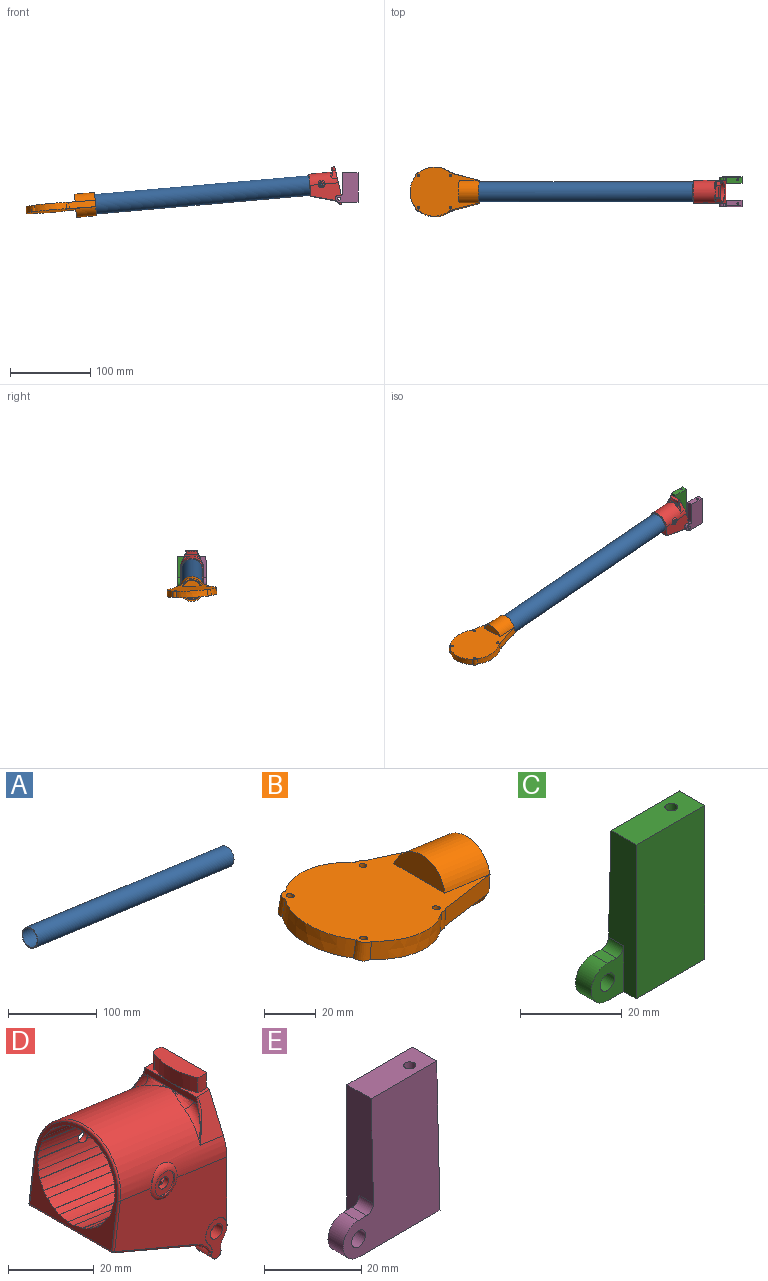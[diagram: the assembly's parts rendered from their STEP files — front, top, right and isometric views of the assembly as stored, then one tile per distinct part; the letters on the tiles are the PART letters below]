
ASSEMBLY  parts=5 mates=2
PART A: 4 faces, bbox 316.9x25x68.8 mm
  f0: cylinder r=12.5mm len=316.9mm, axis (0.99,0,-0.14), area 24857.9mm2, adj f1,f3
  f1: plane 25x24.76mm, normal (0.99,0,-0.14), area 75.4mm2, adj f0,f2
  f2: cylinder r=11.5mm len=316.62mm, axis (0.99,0,-0.14), area 22869.2mm2, adj f1,f3
  f3: plane 25x24.76mm, normal (-0.99,0,0.14), area 75.4mm2, adj f0,f2
PART B: 22 faces, bbox 88.7x62x32.2 mm
  f0: plane 85.74x61.16mm, normal (0.14,0,0.99), area 3234.5mm2, adj f2,f3,f4,f5,f6,f7,f8,f9
  f1: plane 86.15x62mm, normal (-0.14,0,-0.99), area 3325.5mm2, adj f2,f3,f4,f5,f6,f7,f8,f9
  f2: cone r=4mm half-angle=3deg, axis (-0.14,0,-0.99), area 59.2mm2, adj f0,f1,f3,f14
  f3: cone r=31mm half-angle=3deg, axis (-0.14,0,-0.99), area 337.2mm2, adj f0,f1,f2,f4
  f4: cone r=4mm half-angle=3deg, axis (-0.14,0,-0.99), area 59.2mm2, adj f0,f1,f3,f5
  f5: cone r=31mm half-angle=3deg, axis (-0.14,0,-0.99), area 337.2mm2, adj f0,f1,f4,f6
  f6: cone r=4mm half-angle=3deg, axis (-0.14,0,-0.99), area 30.1mm2, adj f0,f1,f5,f7
  f7: plane 33.82x12.55mm, normal (0.25,-0.97,0.02), area 274mm2, adj f0,f1,f6,f8
  f8: plane 29x28.72mm, normal (0.99,0,-0.14), area 169.2mm2, adj f0,f1,f7,f9,f16,f19,f21
  f9: plane 33.82x12.55mm, normal (0.25,0.97,0.02), area 274mm2, adj f0,f1,f8,f10
  f10: cone r=4mm half-angle=3deg, axis (-0.14,0,-0.99), area 30.1mm2, adj f0,f1,f9,f14
  f11: cylinder r=1.5mm len=8.34mm, axis (-0.14,0,-0.99), area 75.4mm2, adj f0,f1
  f12: cylinder r=1.5mm len=8.34mm, axis (-0.14,0,-0.99), area 75.4mm2, adj f0,f1
  f13: cylinder r=1.5mm len=8.34mm, axis (-0.14,0,-0.99), area 75.4mm2, adj f0,f1
  f14: cone r=31mm half-angle=3deg, axis (-0.14,0,-0.99), area 337.2mm2, adj f0,f1,f2,f10
  f15: cylinder r=1.5mm len=8.34mm, axis (-0.14,0,-0.99), area 75.4mm2, adj f0,f1
  f16: cylinder r=14.5mm len=27.87mm, axis (-0.99,0,0.14), area 936.2mm2, adj f1,f8,f17
  f17: plane 27.87x10.4mm, normal (-0.99,0,0.14), area 215.7mm2, adj f1,f16
  f18: plane 27.87x10.4mm, normal (-0.99,0,0.14), area 215.7mm2, adj f0,f19
  f19: cylinder r=14.5mm len=27.87mm, axis (-0.99,0,0.14), area 936.2mm2, adj f0,f8,f18
  f20: plane 25x24.76mm, normal (0.99,0,-0.14), area 490.9mm2, adj f21
  f21: cylinder r=12.5mm len=28.03mm, axis (0.99,0,-0.14), area 1845.7mm2, adj f8,f20
PART C: 15 faces, bbox 28x8x37 mm
  f0: cylinder r=2mm len=4.43mm, axis (0,-1,0), area 55mm2, adj f3,f9
  f1: plane 37x19mm, normal (0,-1,0), area 703mm2, adj f4,f5,f6,f8
  f2: cylinder r=4.5mm len=9mm, axis (0,-1,0), area 61.9mm2, adj f3,f7,f8,f9
  f3: plane 37x28mm, normal (0,1,0.03), area 763.9mm2, adj f0,f2,f4,f5,f6,f7,f8,f10
  f4: plane 37x8mm, normal (1,0,0), area 277.5mm2, adj f1,f3,f5,f8
  f5: plane 19x7mm, normal (0,0,1), area 128.1mm2, adj f1,f3,f4,f6,f14
  f6: plane 37x7.7mm, normal (-1,0,0), area 229.6mm2, adj f1,f3,f5,f8,f9,f10
  f7: plane 4.26x2.5mm, normal (0,0,1), area 10.6mm2, adj f2,f3,f9,f10
  f8: plane 23.5x8mm, normal (0,0,-1), area 167.3mm2, adj f1,f2,f3,f4,f6,f9,f12
  f9: plane 11x9mm, normal (0,-1,0), area 60.6mm2, adj f0,f2,f6,f7,f8,f10
  f10: cylinder r=2mm len=4.26mm, axis (0,1,0), area 13.3mm2, adj f3,f6,f7,f9
  f11: cone r=0mm half-angle=59deg, axis (0,0,-1), area 5.7mm2, adj f12
  f12: cylinder r=1.25mm len=13.5mm, axis (0,0,-1), area 106mm2, adj f8,f11
  f13: cone r=0mm half-angle=59deg, axis (0,0,1), area 5.7mm2, adj f14
  f14: cylinder r=1.25mm len=13.5mm, axis (0,0,1), area 106mm2, adj f5,f13
PART D: 138 faces, bbox 40.7x34.8x48 mm
  f0: cylinder r=10mm len=5.84mm, axis (0,1,0), area 37.2mm2, adj f1,f36,f119,f130
  f1: cylinder r=1.5mm len=5.1mm, axis (0,1,0), area 23.1mm2, adj f0,f2,f40,f41,f119,f130
  f2: cylinder r=4mm len=5.1mm, axis (0,1,0), area 19.4mm2, adj f1,f35,f41,f119
  f3: plane 13.62x1.92mm, normal (0.14,-0.08,0.99), area 1.4mm2, adj f21,f54,f68,f116
  f4: cylinder r=12.6mm len=13.9mm, axis (-0.99,0,0.14), area 27.5mm2, adj f27,f67,f69,f116
  f5: plane 13.62x1.92mm, normal (-0.14,-0.08,-0.99), area 1.4mm2, adj f22,f54,f68,f116
  f6: plane 13.62x1.92mm, normal (-0.14,0.08,-0.99), area 1.4mm2, adj f7,f13,f27,f117
  f7: cylinder r=12.6mm len=13.9mm, axis (-0.99,0,0.14), area 27.5mm2, adj f6,f8,f27,f117
  f8: plane 13.62x1.92mm, normal (0.14,0.08,0.99), area 1.4mm2, adj f7,f14,f27,f117
  f9: cylinder r=14mm len=37.01mm, axis (-0.99,0,0.14), area 1218.4mm2, adj f28,f29,f30,f52,f53,f109,f110,f114
  f10: cylinder r=12.5mm len=29.79mm, axis (-0.99,0,0.14), area 87.7mm2, adj f27,f54,f57,f100
  f11: cylinder r=12.5mm len=29.93mm, axis (-0.99,0,0.14), area 87.7mm2, adj f27,f54,f97,f102
  f12: cylinder r=12.5mm len=30.05mm, axis (-0.99,0,0.14), area 87.7mm2, adj f27,f54,f94,f99
  f13: cylinder r=12.5mm len=30.11mm, axis (-0.99,0,0.14), area 86.7mm2, adj f6,f27,f54,f91,f96,f117
  f14: cylinder r=12.5mm len=30.11mm, axis (-0.99,0,0.14), area 86.6mm2, adj f8,f27,f54,f88,f93,f117
  f15: cylinder r=12.5mm len=30.05mm, axis (-0.99,0,0.14), area 87.7mm2, adj f27,f54,f85,f90
  f16: cylinder r=12.5mm len=29.93mm, axis (-0.99,0,0.14), area 87.7mm2, adj f27,f54,f82,f87
  f17: cylinder r=12.5mm len=29.79mm, axis (-0.99,0,0.14), area 87.7mm2, adj f27,f54,f79,f84
  f18: cylinder r=12.5mm len=29.79mm, axis (-0.99,0,0.14), area 87.7mm2, adj f27,f54,f76,f81
  f19: cylinder r=12.5mm len=29.93mm, axis (-0.99,0,0.14), area 87.7mm2, adj f27,f54,f73,f78
  f20: cylinder r=12.5mm len=30.05mm, axis (-0.99,0,0.14), area 87.7mm2, adj f27,f54,f70,f75
  f21: cylinder r=12.5mm len=30.11mm, axis (-0.99,0,0.14), area 86.6mm2, adj f3,f27,f54,f67,f72,f116
  f22: cylinder r=12.5mm len=30.11mm, axis (-0.99,0,0.14), area 86.7mm2, adj f5,f27,f54,f64,f69,f116
  f23: cylinder r=12.5mm len=30.05mm, axis (-0.99,0,0.14), area 87.7mm2, adj f27,f54,f61,f66
  f24: cylinder r=12.5mm len=29.93mm, axis (-0.99,0,0.14), area 87.7mm2, adj f27,f54,f58,f63
  f25: cylinder r=12.5mm len=29.79mm, axis (-0.99,0,0.14), area 87.7mm2, adj f27,f54,f55,f60
  f26: cylinder r=12.5mm len=25.51mm, axis (-0.99,0,0.14), area 279mm2, adj f106,f137
  f27: plane 27x26.85mm, normal (-0.99,0,0.14), area 159.8mm2, adj f4,f6,f7,f8,f10,f11,f12,f13
  f28: plane 36.95x29.79mm, normal (0,1,0), area 620.1mm2, adj f9,f30,f35,f40,f109,f130,f133,f136
  f29: plane 36.95x29.79mm, normal (0,-1,0), area 620.1mm2, adj f9,f30,f35,f43,f115,f127,f128,f131
  f30: plane 40.17x28.02mm, normal (1,0,0), area 451.6mm2, adj f9,f28,f29,f31,f34,f35,f45,f49
  f31: plane 8.53x4.52mm, normal (0,0,1), area 7.9mm2, adj f30,f32,f48,f49,f53,f125
  f32: plane 17.95x1.83mm, normal (-1,0,0), area 29.3mm2, adj f31,f33,f34,f51,f122,f123,f125,f126
  f33: plane 1.3x0.8mm, normal (-0.99,0,0.14), area 0.4mm2, adj f32,f124,f125
  f34: plane 8.53x4.52mm, normal (0,0,1), area 7.8mm2, adj f30,f32,f45,f46,f47,f48,f52,f126
  f35: cylinder r=3.5mm len=28.2mm, axis (0,1,0), area 179.8mm2, adj f2,f28,f29,f30,f39,f40,f41,f43
  f36: plane 31.51x27mm, normal (-0.39,0,-0.92), area 876.8mm2, adj f0,f37,f118,f119,f120,f128,f132,f133
  f37: cylinder r=10mm len=5.84mm, axis (0,1,0), area 37.2mm2, adj f36,f38,f120,f127
  f38: cylinder r=1.5mm len=5.1mm, axis (0,1,0), area 23.1mm2, adj f37,f39,f43,f44,f120,f127
  f39: cylinder r=4mm len=5.1mm, axis (0,1,0), area 19.4mm2, adj f35,f38,f44,f120
  f40: cylinder r=4mm len=3.5mm, axis (0,1,0), area 0.4mm2, adj f1,f28,f35,f41,f130
  f41: plane 11.2x7mm, normal (0,1,0), area 38.3mm2, adj f1,f2,f35,f40,f42
  f42: cylinder r=2mm len=28.2mm, axis (0,1,0), area 354.4mm2, adj f41,f44
  f43: cylinder r=4mm len=3.5mm, axis (0,1,0), area 0.4mm2, adj f29,f35,f38,f44,f127
  f44: plane 11.2x7mm, normal (0,-1,0), area 38.3mm2, adj f35,f38,f39,f42,f43
  f45: cylinder r=3.19mm len=4.25mm, axis (0,0,-1), area 13.3mm2, adj f30,f34,f46,f50
  f46: cylinder r=18.27mm len=4.25mm, axis (0,0,-1), area 1mm2, adj f34,f45,f47,f50
  f47: cylinder r=0.45mm len=4.25mm, axis (0,0,-1), area 4.2mm2, adj f34,f46,f48,f50
  f48: cylinder r=18.27mm len=13.53mm, axis (0,0,-1), area 58.9mm2, adj f31,f34,f47,f49,f50
  f49: cylinder r=3.19mm len=4.25mm, axis (0,0,-1), area 13.3mm2, adj f30,f31,f48,f50
  f50: plane 15.25x4.5mm, normal (0,0,1), area 59.8mm2, adj f30,f45,f46,f47,f48,f49
  f51: plane 1.3x0.8mm, normal (-0.99,0,0.14), area 0.4mm2, adj f32,f121,f126
  f52: plane 10.9x7.66mm, normal (0.05,0.92,0.39), area 60.1mm2, adj f9,f30,f34,f126
  f53: plane 10.9x7.66mm, normal (0.05,-0.92,0.39), area 60.1mm2, adj f9,f30,f31,f125
  f54: plane 25.2x24.95mm, normal (-0.99,0,0.14), area 78.6mm2, adj f3,f5,f10,f11,f12,f13,f14,f15
  f55: plane 29.72x4.27mm, normal (0.01,1,0.08), area 3mm2, adj f25,f27,f54,f56
  f56: cylinder r=12.6mm len=29.71mm, axis (-0.99,0,0.14), area 60.1mm2, adj f27,f54,f55,f57
  f57: plane 29.72x4.27mm, normal (0.01,-1,0.08), area 3mm2, adj f10,f27,f54,f56
  f58: plane 29.72x4.26mm, normal (0.06,0.89,0.45), area 3mm2, adj f24,f27,f54,f59
  f59: cylinder r=12.6mm len=29.81mm, axis (-0.99,0,0.14), area 60.1mm2, adj f27,f54,f58,f60
  f60: plane 29.72x4.27mm, normal (-0.04,-0.95,-0.31), area 3mm2, adj f25,f27,f54,f59
  f61: plane 29.72x4.24mm, normal (0.11,0.65,0.75), area 3mm2, adj f23,f27,f54,f62
  f62: cylinder r=12.6mm len=29.91mm, axis (-0.99,0,0.14), area 60.1mm2, adj f27,f54,f61,f63
  f63: plane 29.72x4.25mm, normal (-0.09,-0.76,-0.64), area 3mm2, adj f24,f27,f54,f62
  f64: plane 29.71x4.21mm, normal (0.13,0.31,0.94), area 3mm2, adj f22,f27,f54,f65
  f65: cylinder r=12.6mm len=29.97mm, axis (-0.99,0,0.14), area 60.1mm2, adj f27,f54,f64,f66
  f66: plane 29.71x4.22mm, normal (-0.12,-0.45,-0.88), area 3mm2, adj f23,f27,f54,f65
  f67: plane 13.62x1.92mm, normal (0.14,-0.08,0.99), area 1.4mm2, adj f4,f21,f27,f116
  f68: cylinder r=12.6mm len=13.9mm, axis (-0.99,0,0.14), area 27.5mm2, adj f3,f5,f54,f116
  f69: plane 13.62x1.92mm, normal (-0.14,-0.08,-0.99), area 1.4mm2, adj f4,f22,f27,f116
  f70: plane 29.71x4.22mm, normal (0.12,-0.45,0.88), area 3mm2, adj f20,f27,f54,f71
  f71: cylinder r=12.6mm len=29.97mm, axis (-0.99,0,0.14), area 60.1mm2, adj f27,f54,f70,f72
  f72: plane 29.71x4.21mm, normal (-0.13,0.31,-0.94), area 3mm2, adj f21,f27,f54,f71
  f73: plane 29.72x4.25mm, normal (0.09,-0.76,0.64), area 3mm2, adj f19,f27,f54,f74
  f74: cylinder r=12.6mm len=29.91mm, axis (-0.99,0,0.14), area 60.1mm2, adj f27,f54,f73,f75
  f75: plane 29.72x4.24mm, normal (-0.11,0.65,-0.75), area 3mm2, adj f20,f27,f54,f74
  f76: plane 29.72x4.27mm, normal (0.04,-0.95,0.31), area 3mm2, adj f18,f27,f54,f77
  f77: cylinder r=12.6mm len=29.81mm, axis (-0.99,0,0.14), area 60.1mm2, adj f27,f54,f76,f78
  f78: plane 29.72x4.26mm, normal (-0.06,0.89,-0.45), area 3mm2, adj f19,f27,f54,f77
  f79: plane 29.72x4.27mm, normal (-0.01,-1,-0.08), area 3mm2, adj f17,f27,f54,f80
  f80: cylinder r=12.6mm len=29.71mm, axis (-0.99,0,0.14), area 60.1mm2, adj f27,f54,f79,f81
  f81: plane 29.72x4.27mm, normal (-0.01,1,-0.08), area 3mm2, adj f18,f27,f54,f80
  f82: plane 29.72x4.26mm, normal (-0.06,-0.89,-0.45), area 3mm2, adj f16,f27,f54,f83
  f83: cylinder r=12.6mm len=29.81mm, axis (-0.99,0,0.14), area 60.1mm2, adj f27,f54,f82,f84
  f84: plane 29.72x4.27mm, normal (0.04,0.95,0.31), area 3mm2, adj f17,f27,f54,f83
  f85: plane 29.72x4.24mm, normal (-0.11,-0.65,-0.75), area 3mm2, adj f15,f27,f54,f86
  f86: cylinder r=12.6mm len=29.91mm, axis (-0.99,0,0.14), area 60.1mm2, adj f27,f54,f85,f87
  f87: plane 29.72x4.25mm, normal (0.09,0.76,0.64), area 3mm2, adj f16,f27,f54,f86
  f88: plane 29.71x4.21mm, normal (-0.13,-0.31,-0.94), area 3mm2, adj f14,f27,f54,f89
  f89: cylinder r=12.6mm len=29.97mm, axis (-0.99,0,0.14), area 60.1mm2, adj f27,f54,f88,f90
  f90: plane 29.71x4.22mm, normal (0.12,0.45,0.88), area 3mm2, adj f15,f27,f54,f89
  f91: plane 13.62x1.92mm, normal (-0.14,0.08,-0.99), area 1.4mm2, adj f13,f54,f92,f117
  f92: cylinder r=12.6mm len=13.9mm, axis (-0.99,0,0.14), area 27.5mm2, adj f54,f91,f93,f117
  f93: plane 13.62x1.92mm, normal (0.14,0.08,0.99), area 1.4mm2, adj f14,f54,f92,f117
  f94: plane 29.71x4.22mm, normal (-0.12,0.45,-0.88), area 3mm2, adj f12,f27,f54,f95
  f95: cylinder r=12.6mm len=29.97mm, axis (-0.99,0,0.14), area 60.1mm2, adj f27,f54,f94,f96
  f96: plane 29.71x4.21mm, normal (0.13,-0.31,0.94), area 3mm2, adj f13,f27,f54,f95
  f97: plane 29.72x4.25mm, normal (-0.09,0.76,-0.64), area 3mm2, adj f11,f27,f54,f98
  f98: cylinder r=12.6mm len=29.91mm, axis (-0.99,0,0.14), area 60.1mm2, adj f27,f54,f97,f99
  f99: plane 29.72x4.24mm, normal (0.11,-0.65,0.75), area 3mm2, adj f12,f27,f54,f98
  f100: plane 29.72x4.27mm, normal (-0.04,0.95,-0.31), area 3mm2, adj f10,f27,f54,f101
  f101: cylinder r=12.6mm len=29.81mm, axis (-0.99,0,0.14), area 60.1mm2, adj f27,f54,f100,f102
  f102: plane 29.72x4.26mm, normal (0.06,-0.89,0.45), area 3mm2, adj f11,f27,f54,f101
  f103: cylinder r=11.5mm len=23mm, axis (-0.99,0,0.14), area 108.4mm2, adj f54,f107
  f104: plane 22x21.79mm, normal (-0.99,0,0.14), area 66mm2, adj f105,f107
  f105: cylinder r=10mm len=20.34mm, axis (-0.99,0,0.14), area 241.5mm2, adj f104,f106
  f106: plane 25x24.76mm, normal (0.99,0,-0.14), area 176.7mm2, adj f26,f105
  f107: cone r=11mm half-angle=45deg, axis (0.99,0,-0.14), area 50mm2, adj f103,f104
  f108: cylinder r=3.25mm len=6.5mm, axis (0,-1,0), area 8.7mm2, adj f109,f111
  f109: torus R=3.25mm, axis (0,-1,0), area 35.6mm2, adj f9,f28,f108,f110
  f110: plane 1.1x0.15mm, normal (0,-1,0), area 0mm2, adj f9,f109
  f111: plane 6.5x6.5mm, normal (0,1,0), area 25.1mm2, adj f108,f117
  f112: cylinder r=3.25mm len=6.5mm, axis (0,-1,0), area 8.7mm2, adj f113,f115
  f113: plane 6.5x6.5mm, normal (0,-1,0), area 25.1mm2, adj f112,f116
  f114: plane 1.1x0.15mm, normal (0,1,0), area 0mm2, adj f9,f115
  f115: torus R=3.25mm, axis (0,-1,0), area 35.6mm2, adj f9,f29,f112,f114
  f116: cylinder r=1.6mm len=3.2mm, axis (0,1,0), area 14.2mm2, adj f3,f4,f5,f21,f22,f67,f68,f69
  f117: cylinder r=1.6mm len=3.2mm, axis (0,1,0), area 14.2mm2, adj f6,f7,f8,f13,f14,f91,f92,f93
  f118: cylinder r=4mm len=18mm, axis (0,-1,0), area 11mm2, adj f35,f36,f119,f120
  f119: plane 9.46x6.83mm, normal (0,-1,0), area 17.1mm2, adj f0,f1,f2,f35,f36,f118
  f120: plane 9.46x6.83mm, normal (0,1,0), area 17.1mm2, adj f35,f36,f37,f38,f39,f118
  f121: torus R=16mm, axis (0.99,0,-0.14), area 17.2mm2, adj f9,f51,f122,f126
  f122: bspline ~7.75x2.22mm, area 7.1mm2, adj f9,f32,f121
  f123: bspline ~7.75x2.22mm, area 7.1mm2, adj f9,f32,f124
  f124: torus R=16mm, axis (0.99,0,-0.14), area 17.2mm2, adj f9,f33,f123,f125
  f125: bspline ~10.1x5.09mm, area 4.8mm2, adj f31,f32,f33,f53,f124
  f126: bspline ~10.1x5.09mm, area 4.8mm2, adj f32,f34,f51,f52,f121
  f127: torus R=10.5mm, axis (0,-1,0), area 6.1mm2, adj f29,f37,f38,f43,f128
  f128: cylinder r=0.5mm len=26.91mm, axis (-0.92,0,0.39), area 22.8mm2, adj f29,f36,f127,f129
  f129: sphere r=0.5mm, area 0.2mm2, adj f128,f131,f132
  f130: torus R=10.5mm, axis (0,-1,0), area 6.1mm2, adj f0,f1,f28,f40,f133
  f131: cylinder r=0.5mm len=13.55mm, axis (0.14,0,0.99), area 10.7mm2, adj f27,f29,f129,f134
  f132: cylinder r=0.5mm len=27mm, axis (0,1,0), area 17.7mm2, adj f27,f36,f129,f135
  f133: cylinder r=0.5mm len=26.91mm, axis (0.92,0,-0.39), area 22.8mm2, adj f28,f36,f130,f135
  f134: torus R=13.5mm, axis (0.99,0,-0.14), area 34.1mm2, adj f9,f27,f131,f136
  f135: sphere r=0.5mm, area 0.2mm2, adj f132,f133,f136
  f136: cylinder r=0.5mm len=13.55mm, axis (-0.14,0,-0.99), area 10.7mm2, adj f27,f28,f134,f135
  f137: bspline ~26.26x26mm, area 62.9mm2, adj f26,f30
PART E: 15 faces, bbox 28x8x37 mm
  f0: cylinder r=2mm len=4.43mm, axis (0,1,0), area 55mm2, adj f3,f9
  f1: plane 37x19mm, normal (0,1,0), area 703mm2, adj f4,f5,f6,f8
  f2: cylinder r=4.5mm len=9mm, axis (0,1,0), area 61.9mm2, adj f3,f7,f8,f9
  f3: plane 37x28mm, normal (0,-1,0.03), area 763.9mm2, adj f0,f2,f4,f5,f6,f7,f8,f10
  f4: plane 37x8mm, normal (1,0,0), area 277.5mm2, adj f1,f3,f5,f8
  f5: plane 19x7mm, normal (0,0,1), area 128.1mm2, adj f1,f3,f4,f6,f14
  f6: plane 37x7.7mm, normal (-1,0,0), area 229.6mm2, adj f1,f3,f5,f8,f9,f10
  f7: plane 4.26x2.5mm, normal (0,0,1), area 10.6mm2, adj f2,f3,f9,f10
  f8: plane 23.5x8mm, normal (0,0,-1), area 167.3mm2, adj f1,f2,f3,f4,f6,f9,f12
  f9: plane 11x9mm, normal (0,1,0), area 60.6mm2, adj f0,f2,f6,f7,f8,f10
  f10: cylinder r=2mm len=4.26mm, axis (0,-1,0), area 13.3mm2, adj f3,f6,f7,f9
  f11: cone r=0mm half-angle=59deg, axis (0,0,-1), area 5.7mm2, adj f12
  f12: cylinder r=1.25mm len=13.5mm, axis (0,0,-1), area 106mm2, adj f8,f11
  f13: cone r=0mm half-angle=59deg, axis (0,0,1), area 5.7mm2, adj f14
  f14: cylinder r=1.25mm len=13.5mm, axis (0,0,1), area 106mm2, adj f5,f13
PLACE A rot(axis=(0,-1,0),13deg) t=(0,0,0)mm
PLACE B rot(axis=(-0.23,-0.97,0.01),13.3deg) t=(0,-1.03,0.03)mm
PLACE C at identity
PLACE D rot(axis=(0,-1,0),13deg) t=(0,0,0)mm
PLACE E at identity fixed
MATE planar E.f8 <-> C.f8  axis (0,0,-1) through (12.67,-14.7,-4.5)mm
MATE revolute A.f0 <-> B.f21  axis (-1,0,-0.09) through (-327.12,0,-8.78)mm
